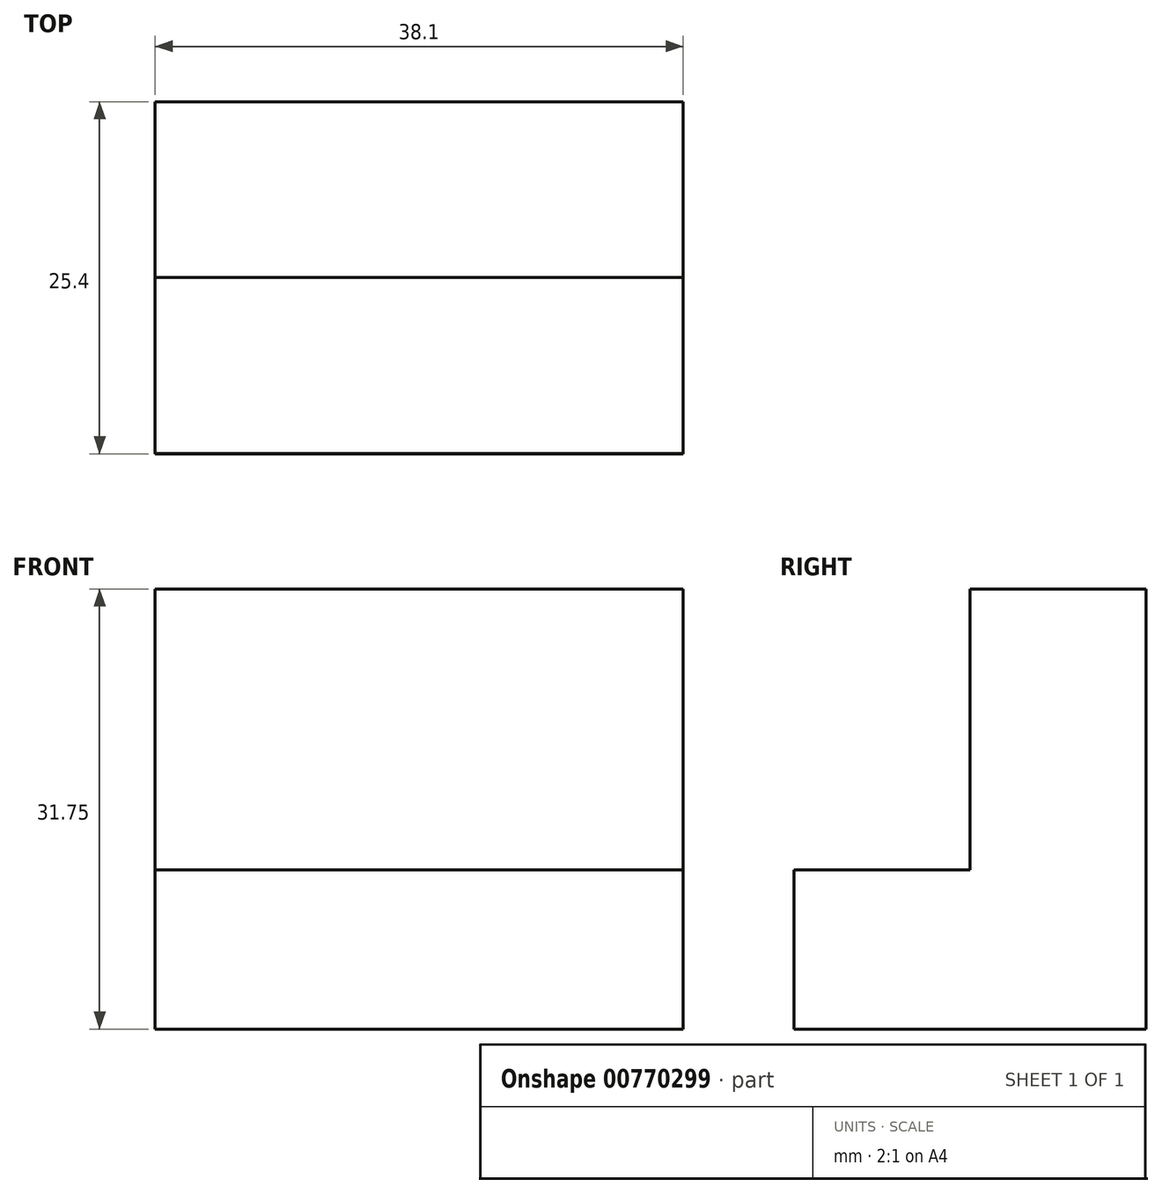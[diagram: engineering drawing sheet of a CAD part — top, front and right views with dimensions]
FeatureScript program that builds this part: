
annotation { "Feature Type Name" : "Feature", "Feature Type Description" : "" }
export const myFeature = defineFeature(function(context is Context, id is Id, definition is map)
    precondition{}
    {
        {
            var Q0;
            Q0=qCreatedBy(makeId("Front.planeOp"),FACE);
            var sketch = newSketch(context, id + "F0", { "sketchPlane" : qUnion([Q0])});
            skLineSegment(sketch, "E0", {"start": v(0, 0) * mm, "end": v(38.1, 0) * mm});
            skLineSegment(sketch, "E1", {"start": v(38.1, 0) * mm, "end": v(38.1, 38.1) * mm});
            skLineSegment(sketch, "E2", {"start": v(38.1, 38.1) * mm, "end": v(0, 38.1) * mm});
            skLineSegment(sketch, "E3", {"start": v(0, 38.1) * mm, "end": v(0, 0) * mm});
            skSolve(sketch);
        }
        {
            var Q0;
            Q0 = qSketchRegion(id + "F0", true);
            extrude(context, id + "F1", {"entities" : qUnion([Q0]), "depth" : 25.4 * mm, "offsetDistance" : 25.4 * mm});
        }
        {
            var Q0;
            Q0=makeQuery(id+"F1.opExtrude","SWEPT_FACE",FACE,{"disambiguationData":[OSD([sQuery(id+"F0.wireOp",EDGE,"E1")])]});
            var sketch = newSketch(context, id + "F2", { "sketchPlane" : qUnion([Q0])});
            skLineSegment(sketch, "E4", {"start": v(-12.7, 38.16) * mm, "end": v(-12.7, 11.5) * mm});
            skLineSegment(sketch, "E5", {"start": v(-12.7, 11.5) * mm, "end": v(-25.4, 11.5) * mm});
            skLineSegment(sketch, "E6", {"start": v(-25.4, 11.5) * mm, "end": v(-90.16, 53.8) * mm});
            skLineSegment(sketch, "E7", {"start": v(-12.7, 38.16) * mm, "end": v(-80.48, 82.15) * mm});
            skSolve(sketch);
        }
        {
            var Q0;
            {var subQ1=sQuery(id+"F2.wireOp",EDGE,"E5");Q0=makeQuery(id+"F2.imprint","IMPRINT",FACE,{"disambiguationData":[TD([[makeQuery(id+"F2.imprint","IMPRINT",EDGE,{"derivedFrom":subQ1}),-1.0]])]});}
            extrude(context, id + "F3", {"entities" : qUnion([Q0]), "operationType" : NewBodyOperationType.REMOVE, "oppositeDirection" : true, "depth" : 50.8 * mm, "offsetDistance" : 25.4 * mm});
        }
        {
            var Q0;
            Q0=makeQuery(id+"F1.opExtrude","SWEPT_FACE",FACE,{"disambiguationData":[OSD([sQuery(id+"F0.wireOp",EDGE,"E2")])]});
            extrude(context, id + "F4", {"entities" : qUnion([Q0]), "operationType" : NewBodyOperationType.REMOVE, "oppositeDirection" : true, "depth" : 6.35 * mm, "offsetDistance" : 25.4 * mm});
        }
    });
